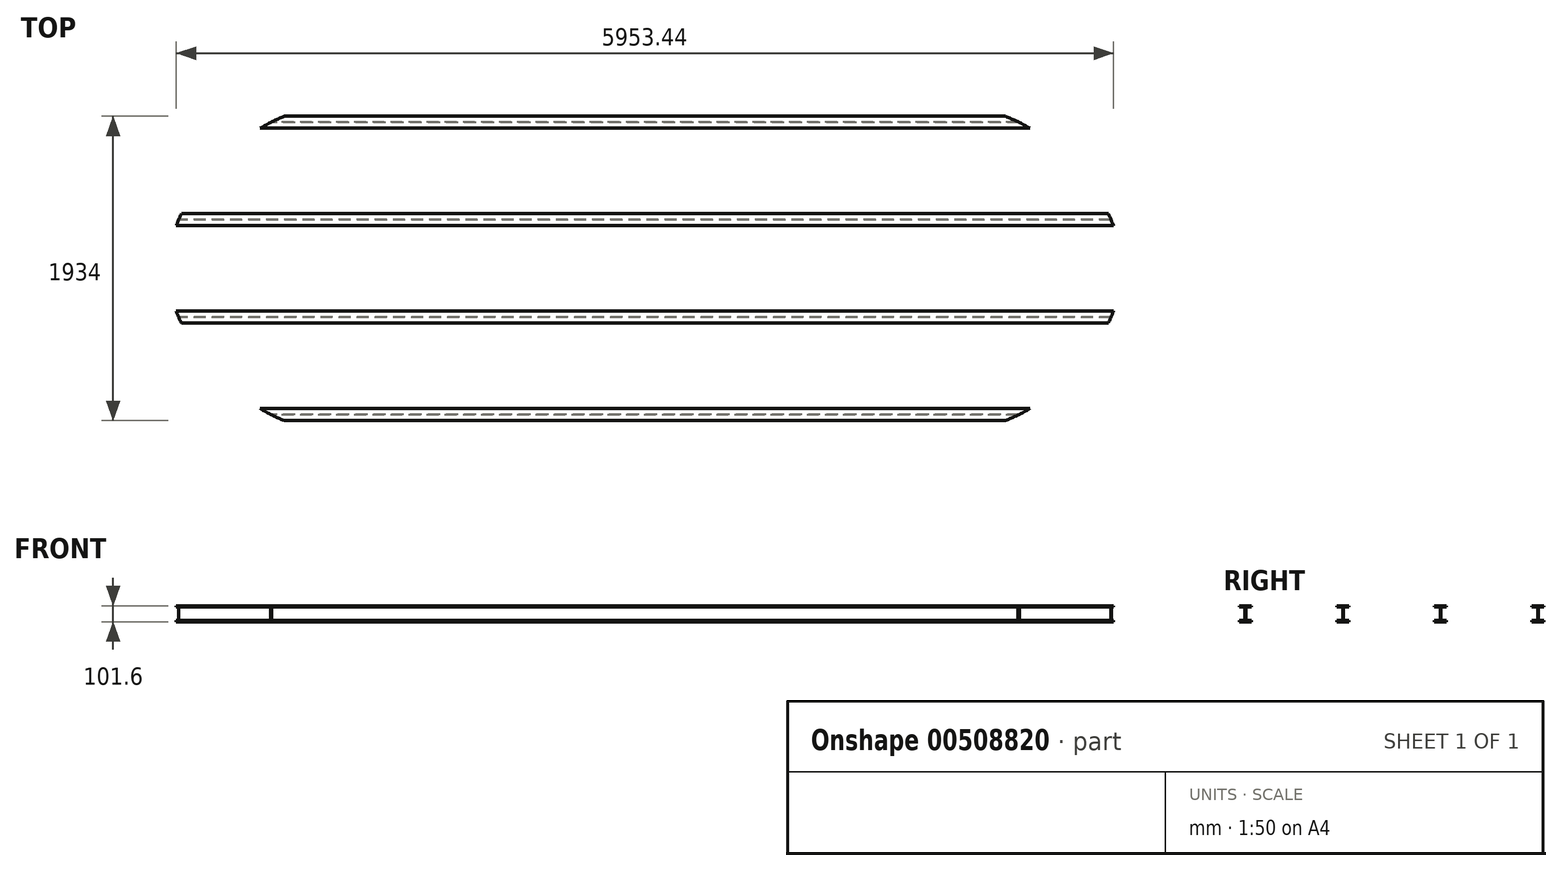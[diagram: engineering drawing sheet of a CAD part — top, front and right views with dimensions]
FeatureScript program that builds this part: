
annotation { "Feature Type Name" : "Feature", "Feature Type Description" : "" }
export const myFeature = defineFeature(function(context is Context, id is Id, definition is map)
    precondition{}
    {
        {
            var Q0;
            Q0=qCreatedBy(makeId("Right.planeOp"),FACE);
            var sketch = newSketch(context, id + "F0", { "sketchPlane" : qUnion([Q0])});
            skLineSegment(sketch, "E0", {"start": v(-967, 0) * mm, "end": v(-890.8, 0) * mm});
            skLineSegment(sketch, "E1", {"start": v(-890.8, 0) * mm, "end": v(-890.8, -7.37) * mm});
            skLineSegment(sketch, "E2", {"start": v(-890.8, -7.37) * mm, "end": v(-926.74, -7.37) * mm});
            skLineSegment(sketch, "E3", {"start": v(-926.74, -7.37) * mm, "end": v(-926.74, -94.23) * mm});
            skLineSegment(sketch, "E4", {"start": v(-926.74, -94.23) * mm, "end": v(-890.8, -94.23) * mm});
            skLineSegment(sketch, "E5", {"start": v(-890.8, -94.23) * mm, "end": v(-890.8, -101.6) * mm});
            skLineSegment(sketch, "E6", {"start": v(-890.8, -101.6) * mm, "end": v(-967, -101.6) * mm});
            skLineSegment(sketch, "E7", {"start": v(-967, -101.6) * mm, "end": v(-967, -94.23) * mm});
            skLineSegment(sketch, "E8", {"start": v(-967, -94.23) * mm, "end": v(-931.06, -94.23) * mm});
            skLineSegment(sketch, "E9", {"start": v(-931.06, -94.23) * mm, "end": v(-931.06, -7.37) * mm});
            skLineSegment(sketch, "E10", {"start": v(-931.06, -7.37) * mm, "end": v(-967, -7.37) * mm});
            skLineSegment(sketch, "E11", {"start": v(-967, -7.37) * mm, "end": v(-967, 0) * mm});
            skLineSegment(sketch, "E12.1.0.0", {"start": v(-311.8, -94.23) * mm, "end": v(-311.8, -7.37) * mm});
            skLineSegment(sketch, "E12.1.0.1", {"start": v(-307.47, -7.37) * mm, "end": v(-307.47, -94.23) * mm});
            skLineSegment(sketch, "E12.1.0.2", {"start": v(-347.73, -94.23) * mm, "end": v(-311.8, -94.23) * mm});
            skLineSegment(sketch, "E12.1.0.3", {"start": v(-347.73, -101.6) * mm, "end": v(-347.73, -94.23) * mm});
            skLineSegment(sketch, "E12.1.0.4", {"start": v(-271.53, -101.6) * mm, "end": v(-347.73, -101.6) * mm});
            skLineSegment(sketch, "E12.1.0.5", {"start": v(-271.53, -94.23) * mm, "end": v(-271.53, -101.6) * mm});
            skLineSegment(sketch, "E12.1.0.6", {"start": v(-307.47, -94.23) * mm, "end": v(-271.53, -94.23) * mm});
            skLineSegment(sketch, "E12.1.0.7", {"start": v(-271.53, -7.37) * mm, "end": v(-307.47, -7.37) * mm});
            skLineSegment(sketch, "E12.1.0.8", {"start": v(-271.53, 0) * mm, "end": v(-271.53, -7.37) * mm});
            skLineSegment(sketch, "E12.1.0.9", {"start": v(-347.73, 0) * mm, "end": v(-271.53, 0) * mm});
            skLineSegment(sketch, "E12.1.0.10", {"start": v(-347.73, -7.37) * mm, "end": v(-347.73, 0) * mm});
            skLineSegment(sketch, "E12.1.0.11", {"start": v(-311.8, -7.37) * mm, "end": v(-347.73, -7.37) * mm});
            skLineSegment(sketch, "E12.2.0.0", {"start": v(307.47, -94.23) * mm, "end": v(307.47, -7.37) * mm});
            skLineSegment(sketch, "E12.2.0.1", {"start": v(311.8, -7.37) * mm, "end": v(311.8, -94.23) * mm});
            skLineSegment(sketch, "E12.2.0.2", {"start": v(271.53, -94.23) * mm, "end": v(307.47, -94.23) * mm});
            skLineSegment(sketch, "E12.2.0.3", {"start": v(271.53, -101.6) * mm, "end": v(271.53, -94.23) * mm});
            skLineSegment(sketch, "E12.2.0.4", {"start": v(347.73, -101.6) * mm, "end": v(271.53, -101.6) * mm});
            skLineSegment(sketch, "E12.2.0.5", {"start": v(347.73, -94.23) * mm, "end": v(347.73, -101.6) * mm});
            skLineSegment(sketch, "E12.2.0.6", {"start": v(311.8, -94.23) * mm, "end": v(347.73, -94.23) * mm});
            skLineSegment(sketch, "E12.2.0.7", {"start": v(347.73, -7.37) * mm, "end": v(311.8, -7.37) * mm});
            skLineSegment(sketch, "E12.2.0.8", {"start": v(347.73, 0) * mm, "end": v(347.73, -7.37) * mm});
            skLineSegment(sketch, "E12.2.0.9", {"start": v(271.53, 0) * mm, "end": v(347.73, 0) * mm});
            skLineSegment(sketch, "E12.2.0.10", {"start": v(271.53, -7.37) * mm, "end": v(271.53, 0) * mm});
            skLineSegment(sketch, "E12.2.0.11", {"start": v(307.47, -7.37) * mm, "end": v(271.53, -7.37) * mm});
            skLineSegment(sketch, "E12.direction1", {"start": v(-347.73, -101.6) * mm, "end": v(-967, -101.6) * mm, "construction": true});
            skLineSegment(sketch, "E13.0.3.0", {"start": v(926.74, -94.23) * mm, "end": v(926.74, -7.37) * mm});
            skLineSegment(sketch, "E13.3.3.0", {"start": v(931.06, -7.37) * mm, "end": v(931.06, -94.23) * mm});
            skLineSegment(sketch, "E13.6.3.0", {"start": v(890.8, -94.23) * mm, "end": v(926.74, -94.23) * mm});
            skLineSegment(sketch, "E13.9.3.0", {"start": v(890.8, -101.6) * mm, "end": v(890.8, -94.23) * mm});
            skLineSegment(sketch, "E13.12.3.0", {"start": v(967, -101.6) * mm, "end": v(890.8, -101.6) * mm});
            skLineSegment(sketch, "E13.15.3.0", {"start": v(967, -94.23) * mm, "end": v(967, -101.6) * mm});
            skLineSegment(sketch, "E13.18.3.0", {"start": v(931.06, -94.23) * mm, "end": v(967, -94.23) * mm});
            skLineSegment(sketch, "E13.21.3.0", {"start": v(967, -7.37) * mm, "end": v(931.06, -7.37) * mm});
            skLineSegment(sketch, "E13.24.3.0", {"start": v(967, 0) * mm, "end": v(967, -7.37) * mm});
            skLineSegment(sketch, "E13.27.3.0", {"start": v(890.8, 0) * mm, "end": v(967, 0) * mm});
            skLineSegment(sketch, "E13.30.3.0", {"start": v(890.8, -7.37) * mm, "end": v(890.8, 0) * mm});
            skLineSegment(sketch, "E13.33.3.0", {"start": v(926.74, -7.37) * mm, "end": v(890.8, -7.37) * mm});
            skSolve(sketch);
        }
        {
            var Q0;
            Q0=makeQuery(id+"F0.imprint","IMPRINT",FACE,{"disambiguationData":[TD([[makeQuery(id+"F0.imprint","IMPRINT",EDGE,{"derivedFrom":sQuery(id+"F0.wireOp",EDGE,"E0")}),-1.0]])]});
            var Q1;
            Q1=makeQuery(id+"F0.imprint","IMPRINT",FACE,{"disambiguationData":[TD([[makeQuery(id+"F0.imprint","IMPRINT",EDGE,{"derivedFrom":sQuery(id+"F0.wireOp",EDGE,"E12.1.0.0")}),-1.0]])]});
            var Q2;
            Q2=makeQuery(id+"F0.imprint","IMPRINT",FACE,{"disambiguationData":[TD([[makeQuery(id+"F0.imprint","IMPRINT",EDGE,{"derivedFrom":sQuery(id+"F0.wireOp",EDGE,"E12.2.0.0")}),-1.0]])]});
            var Q3;
            Q3=makeQuery(id+"F0.imprint","IMPRINT",FACE,{"disambiguationData":[TD([[makeQuery(id+"F0.imprint","IMPRINT",EDGE,{"derivedFrom":sQuery(id+"F0.wireOp",EDGE,"E13.0.3.0")}),-1.0]])]});
            extrude(context, id + "F1", {"entities" : qUnion([Q0, Q1, Q2, Q3]), "depth" : 3050 * mm, "offsetDistance" : 25 * mm, "hasSecondDirection" : true, "secondDirectionOppositeDirection" : true, "secondDirectionDepth" : 3050 * mm});
        }
        {
            var Q0;
            Q0=qCreatedBy(makeId("Top.planeOp"),FACE);
            var sketch = newSketch(context, id + "F2", { "sketchPlane" : qUnion([Q0])});
            skArc(sketch, "E14.0.0", {"start": v(3050, 0) * mm, "mid": v(2630, 758.57) * mm, "end": v(1817, 1060) * mm});
            skLineSegment(sketch, "E14.0.1", {"start": v(1817, 1060) * mm, "end": v(-1817, 1060) * mm});
            skArc(sketch, "E14.0.2", {"start": v(-1817, 1060) * mm, "mid": v(-2630, 758.57) * mm, "end": v(-3050, 0) * mm});
            skArc(sketch, "E14.0.3", {"start": v(-3050, 0) * mm, "mid": v(-2630, -758.57) * mm, "end": v(-1817, -1060) * mm});
            skLineSegment(sketch, "E14.0.4", {"start": v(-1817, -1060) * mm, "end": v(1817, -1060) * mm});
            skArc(sketch, "E14.0.5", {"start": v(1817, -1060) * mm, "mid": v(2630, -758.57) * mm, "end": v(3050, 0) * mm});
            skLineSegment(sketch, "E15", {"start": v(-3050, 0) * mm, "end": v(3050, 0) * mm, "construction": true});
            skLineSegment(sketch, "E16.bottom", {"start": v(4240.14, -2338.68) * mm, "end": v(-4240.14, -2338.68) * mm});
            skLineSegment(sketch, "E16.top", {"start": v(4240.14, 2338.68) * mm, "end": v(-4240.14, 2338.68) * mm});
            skLineSegment(sketch, "E16.left", {"start": v(4240.14, -2338.68) * mm, "end": v(4240.14, 2338.68) * mm});
            skLineSegment(sketch, "E16.right", {"start": v(-4240.14, -2338.68) * mm, "end": v(-4240.14, 2338.68) * mm});
            skPoint(sketch, "E16.middle", {"position": v(0, 0) * mm});
            skSolve(sketch);
        }
        {
            var Q0;
            Q0=makeQuery(id+"F2.imprint","IMPRINT",FACE,{"disambiguationData":[TD([[makeQuery(id+"F2.imprint","IMPRINT",EDGE,{"derivedFrom":sQuery(id+"F2.wireOp",EDGE,"E14.0.0")}),-1.0]])]});
            extrude(context, id + "F3", {"entities" : qUnion([Q0]), "operationType" : NewBodyOperationType.REMOVE, "oppositeDirection" : true, "depth" : 155 * mm, "offsetDistance" : 25 * mm});
        }
        {
            var Q0;
            Q0=makeQuery(id+"F1.opExtrude","SWEPT_FACE",FACE,{"disambiguationData":[OSD([sQuery(id+"F0.wireOp",EDGE,"E12.1.0.9")])]});
            var sketch = newSketch(context, id + "F4", { "sketchPlane" : qUnion([Q0])});
            skCircle(sketch, "E17", {"center": v(0, 0) * mm, "radius": 100 * mm});
            skSolve(sketch);
        }
        {
            var Q0;
            Q0=makeQuery(id+"F1.opExtrude","SWEPT_FACE",FACE,{"disambiguationData":[OSD([sQuery(id+"F0.wireOp",EDGE,"E12.1.0.4")])]});
            var sketch = newSketch(context, id + "F5", { "sketchPlane" : qUnion([Q0])});
            skCircle(sketch, "E18", {"center": v(0, 0) * mm, "radius": 225 * mm});
            skSolve(sketch);
        }
    });
